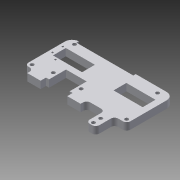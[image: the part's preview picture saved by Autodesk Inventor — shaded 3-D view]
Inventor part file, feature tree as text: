
AUTODESK INVENTOR PART (.ipt)
format: ipt  version: 2013 (Build 170138000, 138)  size: 145,920 bytes
history: native  units: mm
features: extrude x1, sketch x1
ambient origin geometry x8: Origin, YZ Plane, XZ Plane, XY Plane, X Axis, Y Axis, Z Axis, Center Point
bodies: Solid1 (feature_tree)
feature tree (2):
  extrude  "Extrusion1"  [1 undecoded]
  sketch  "Sketch1"  dims[d0=6.0mm d1=0.0mm]
note: 1 required parameter value undecoded (feature->parameter linkage not recoverable at this tier; creation-order binding heuristic only, values carry confidence <= 0.55)
